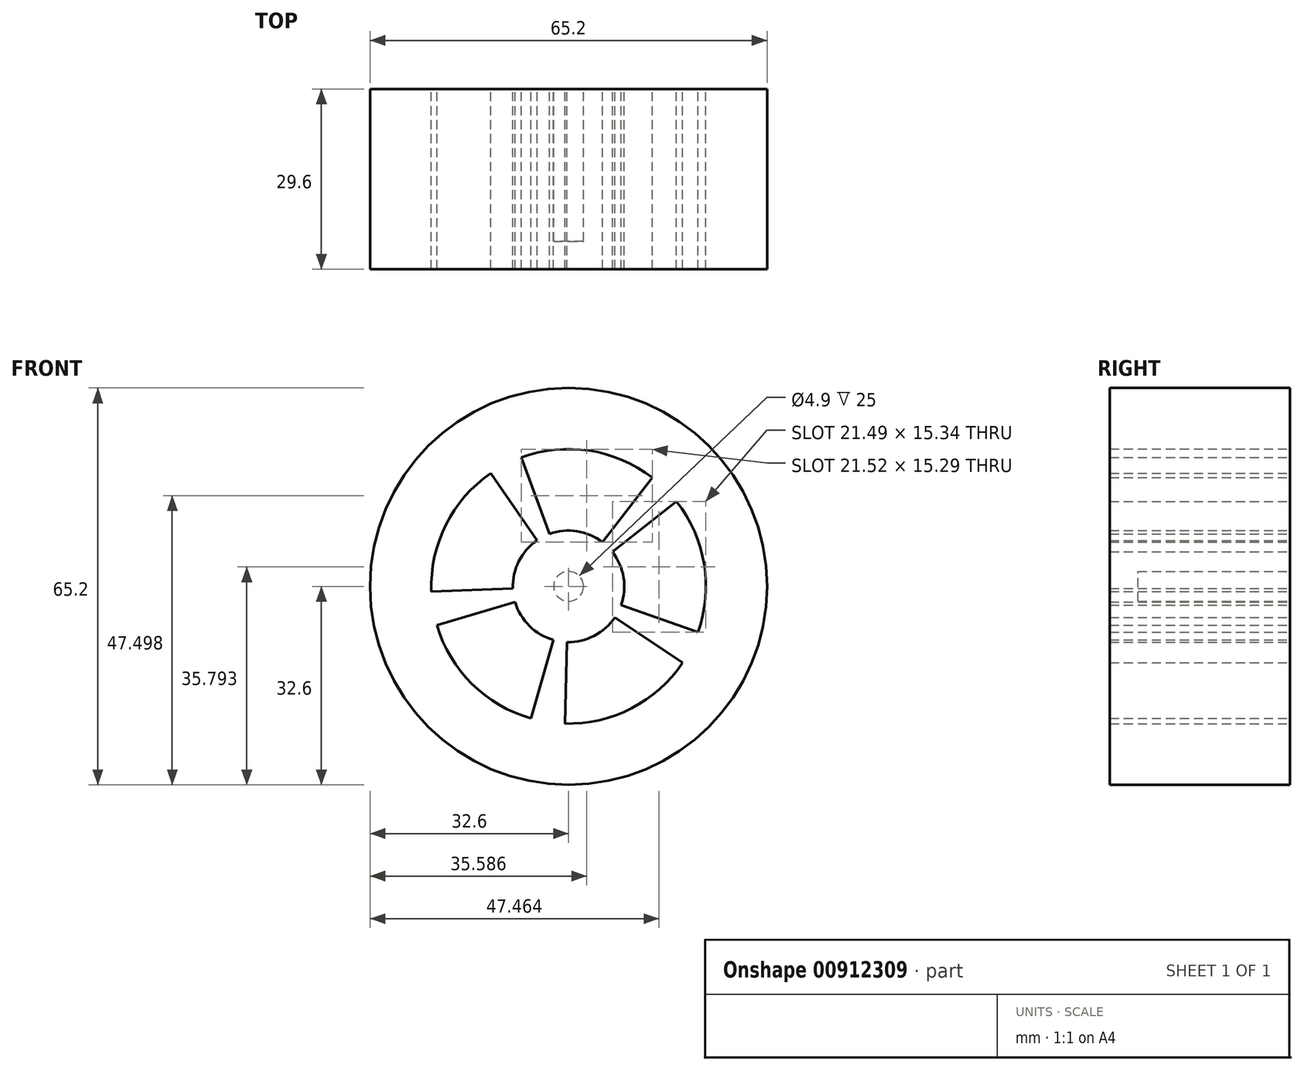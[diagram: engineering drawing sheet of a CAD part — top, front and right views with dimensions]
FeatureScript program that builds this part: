
annotation { "Feature Type Name" : "Feature", "Feature Type Description" : "" }
export const myFeature = defineFeature(function(context is Context, id is Id, definition is map)
    precondition{}
    {
        {
            var Q0;
            Q0=qCreatedBy(makeId("Front.planeOp"),FACE);
            var sketch = newSketch(context, id + "F0", { "sketchPlane" : qUnion([Q0])});
            skCircle(sketch, "E0", {"center": v(0, 0) * mm, "radius": 9.15 * mm});
            skCircle(sketch, "E1", {"center": v(0, 0) * mm, "radius": 4.75 * mm});
            skCircle(sketch, "E2", {"center": v(0, 0) * mm, "radius": 22.55 * mm});
            skLineSegment(sketch, "E3", {"start": v(-12.75, 18.6) * mm, "end": v(-5.17, 7.55) * mm});
            skLineSegment(sketch, "E4", {"start": v(-7.78, 21.17) * mm, "end": v(-3.16, 8.59) * mm});
            skCircle(sketch, "E5", {"center": v(0, 0) * mm, "radius": 32.6 * mm});
            skLineSegment(sketch, "E6.1.0", {"start": v(-21.63, -6.38) * mm, "end": v(-8.78, -2.59) * mm});
            skLineSegment(sketch, "E6.1.1", {"start": v(-22.53, -0.85) * mm, "end": v(-9.14, -0.35) * mm});
            skLineSegment(sketch, "E6.2.0", {"start": v(-0.62, -22.54) * mm, "end": v(-0.25, -9.15) * mm});
            skLineSegment(sketch, "E6.2.1", {"start": v(-6.15, -21.7) * mm, "end": v(-2.5, -8.8) * mm});
            skLineSegment(sketch, "E6.3.0", {"start": v(21.25, -7.55) * mm, "end": v(8.62, -3.06) * mm});
            skLineSegment(sketch, "E6.3.1", {"start": v(18.73, -12.55) * mm, "end": v(7.6, -5.1) * mm});
            skLineSegment(sketch, "E6.4.0", {"start": v(13.75, 17.87) * mm, "end": v(5.58, 7.25) * mm});
            skLineSegment(sketch, "E6.4.1", {"start": v(17.73, 13.94) * mm, "end": v(7.2, 5.65) * mm});
            skSolve(sketch);
        }
        {
            var Q0;
            Q0=makeQuery(id+"F0.imprint","IMPRINT",FACE,{"disambiguationData":[TD([[makeQuery(id+"F0.imprint","IMPRINT",EDGE,{"derivedFrom":sQuery(id+"F0.wireOp",EDGE,"E5")}),1.0]])]});
            var Q1;
            {var subQ0=sQuery(id+"F0.wireOp",EDGE,"E3");Q1=makeQuery(id+"F0.imprint","IMPRINT",FACE,{"disambiguationData":[TD([[makeQuery(id+"F0.imprint","IMPRINT",EDGE,{"derivedFrom":subQ0}),1.0]])]});}
            var Q2;
            {var subQ0=sQuery(id+"F0.wireOp",EDGE,"E6.4.0");Q2=makeQuery(id+"F0.imprint","IMPRINT",FACE,{"disambiguationData":[TD([[makeQuery(id+"F0.imprint","IMPRINT",EDGE,{"derivedFrom":subQ0}),1.0]])]});}
            var Q3;
            {var subQ0=sQuery(id+"F0.wireOp",EDGE,"E6.3.0");Q3=makeQuery(id+"F0.imprint","IMPRINT",FACE,{"disambiguationData":[TD([[makeQuery(id+"F0.imprint","IMPRINT",EDGE,{"derivedFrom":subQ0}),1.0]])]});}
            var Q4;
            {var subQ0=sQuery(id+"F0.wireOp",EDGE,"E6.2.0");Q4=makeQuery(id+"F0.imprint","IMPRINT",FACE,{"disambiguationData":[TD([[makeQuery(id+"F0.imprint","IMPRINT",EDGE,{"derivedFrom":subQ0}),1.0]])]});}
            var Q5;
            {var subQ0=sQuery(id+"F0.wireOp",EDGE,"E6.1.0");Q5=makeQuery(id+"F0.imprint","IMPRINT",FACE,{"disambiguationData":[TD([[makeQuery(id+"F0.imprint","IMPRINT",EDGE,{"derivedFrom":subQ0}),1.0]])]});}
            var Q6;
            Q6=makeQuery(id+"F0.imprint","IMPRINT",FACE,{"disambiguationData":[TD([[makeQuery(id+"F0.imprint","IMPRINT",EDGE,{"derivedFrom":sQuery(id+"F0.wireOp",EDGE,"E1")}),-1.0]])]});
            var Q7;
            Q7=makeQuery(id+"F0.imprint","IMPRINT",FACE,{"disambiguationData":[TD([[makeQuery(id+"F0.imprint","IMPRINT",EDGE,{"derivedFrom":sQuery(id+"F0.wireOp",EDGE,"E1")}),1.0]])]});
            extrude(context, id + "F1", {"entities" : qUnion([Q0, Q1, Q2, Q3, Q4, Q5, Q6, Q7]), "depth" : 29.6 * mm, "offsetDistance" : 25 * mm});
        }
        {
            var Q0;
            Q0=qCreatedBy(makeId("Front.planeOp"),FACE);
            var sketch = newSketch(context, id + "F2", { "sketchPlane" : qUnion([Q0])});
            skCircle(sketch, "E7", {"center": v(0, 0) * mm, "radius": 2.45 * mm});
            skLineSegment(sketch, "E8", {"start": v(17.72, 13.94) * mm, "end": v(7.19, 5.66) * mm});
            skLineSegment(sketch, "E9", {"start": v(5.59, 7.27) * mm, "end": v(13.73, 17.89) * mm});
            skFitSpline(sketch, "E10", {"points": [v(13.73, 17.89) * mm, v(17.72, 13.94) * mm], "startDerivative": vector(4.8, -3.62) * mm, "endDerivative": vector(3.17, -4.41) * mm});
            skFitSpline(sketch, "E11", {"points": [v(5.59, 7.27) * mm, v(7.19, 5.66) * mm], "startDerivative": vector(1.84, -1.08) * mm, "endDerivative": vector(1.29, -1.93) * mm});
            skSolve(sketch);
        }
        {
            var Q0;
            Q0=makeQuery(id+"F2.imprint","IMPRINT",FACE,{"disambiguationData":[TD([[makeQuery(id+"F2.imprint","IMPRINT",EDGE,{"derivedFrom":sQuery(id+"F2.wireOp",EDGE,"E7")}),1.0]])]});
            extrude(context, id + "F3", {"entities" : qUnion([Q0]), "operationType" : NewBodyOperationType.REMOVE, "endBound" : BoundingType.SYMMETRIC, "depth" : 50 * mm, "offsetDistance" : 25 * mm});
        }
    });
